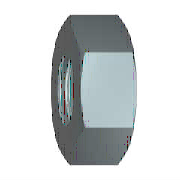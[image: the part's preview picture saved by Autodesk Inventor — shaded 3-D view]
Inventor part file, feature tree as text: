
AUTODESK INVENTOR PART (.ipt)
format: ipt  version: 2024 (Build 280153000, 153)  size: 161,280 bytes
history: native  units: mm (DEFAULTED — no unit token found)
features: chamfer x3, sketch x3, hole x1, other x1, plane x1
ambient origin geometry x7: Origin, YZ Plane, XZ Plane, X Axis, Y Axis, Z Axis, Center Point
bodies: Solid1 (feature_tree), Body (feature_tree)
feature tree (9):
  chamfer  "Chamfer1"  Angle=30.0deg  [1 undecoded]
  hole  "Thread"  [1 undecoded]
  chamfer  "Chamfer2"  Distance=5.9mm
  chamfer  "Chamfer3"  Distance=5.9mm
  other  "Work Axis1"
  plane  "Work Plane1"
  sketch  "Sketch1"  dims[d0=8.082904mm]
  sketch  "Sketch2"  dims[d1=3.2mm]
  sketch  "Sketch3"  dims[d2=0.0mm d3=30.0deg d4=30.0deg d5=5.9mm d6=5.9mm d7=90.0deg d25=3.242mm d26=6.0mm d27=4.0mm d28=2.0mm d29=14.3117mm d30=8.0mm d31=20.594885mm d8=0.378886mm d9=30.0deg d10=0.378886mm d11=30.0deg d13=0.0mm d14=0.0mm d39=0.0mm d40=0.378886mm d41=0.378886mm d42=0.0mm]
note: 2 required parameter values undecoded (feature->parameter linkage not recoverable at this tier; creation-order binding heuristic only, values carry confidence <= 0.55)
